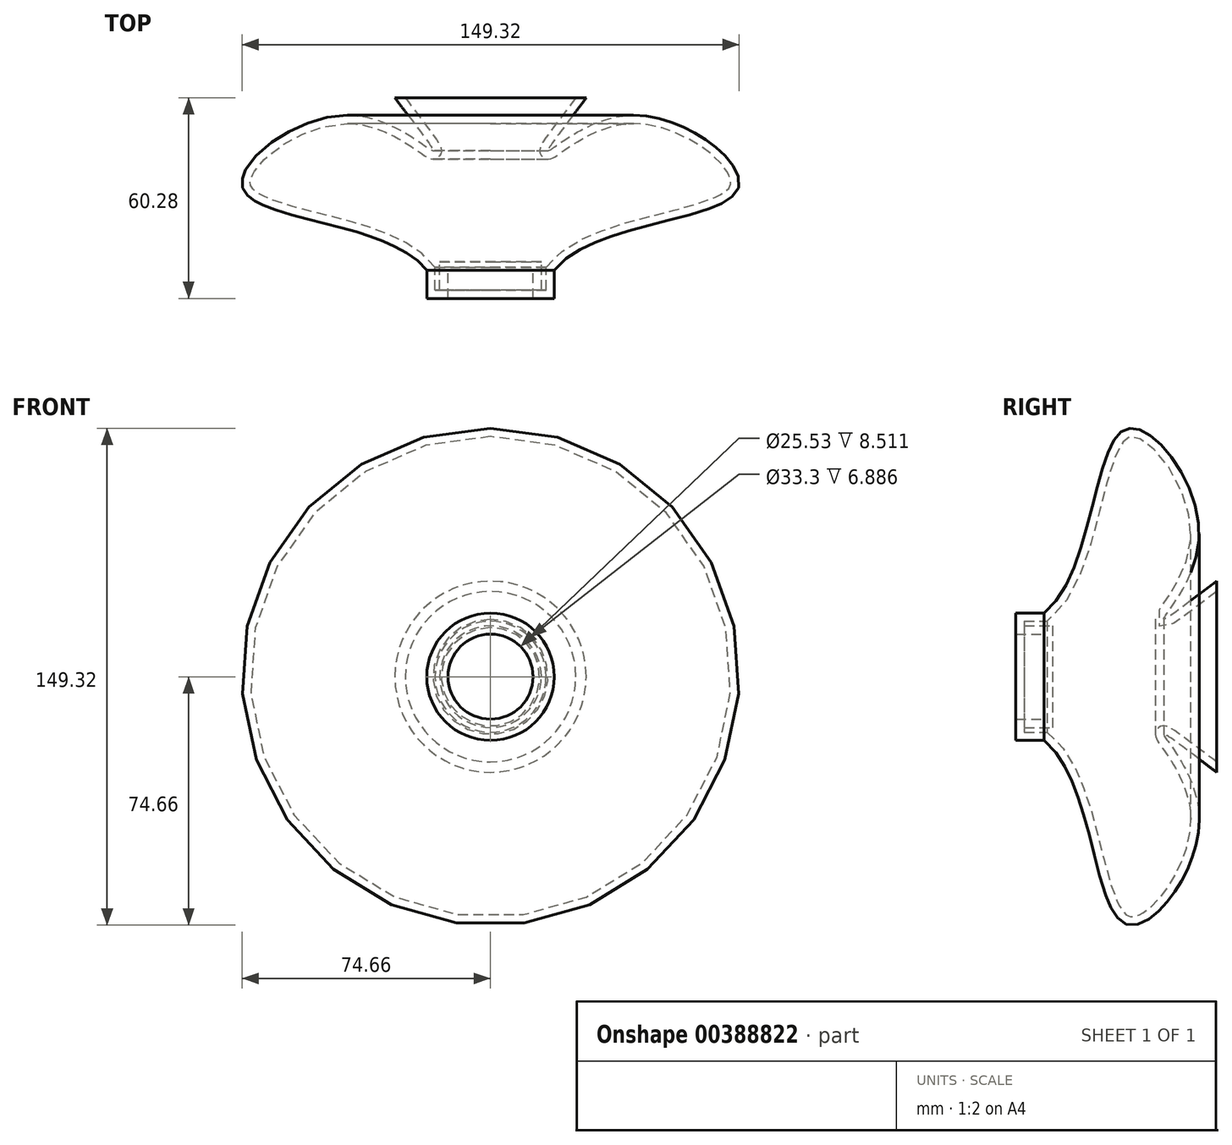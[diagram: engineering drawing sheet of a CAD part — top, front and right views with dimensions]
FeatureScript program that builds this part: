
annotation { "Feature Type Name" : "Feature", "Feature Type Description" : "" }
export const myFeature = defineFeature(function(context is Context, id is Id, definition is map)
    precondition{}
    {
        {
            var Q0;
            Q0=qCreatedBy(makeId("Top.planeOp"),FACE);
            var sketch = newSketch(context, id + "F0", { "sketchPlane" : qUnion([Q0])});
            skLineSegment(sketch, "E0", {"start": v(0, 0) * mm, "end": v(28.72, 0) * mm});
            skLineSegment(sketch, "E1", {"start": v(0, -51.77) * mm, "end": v(12.77, -51.77) * mm});
            skLineSegment(sketch, "E2", {"start": v(12.77, -51.77) * mm, "end": v(12.77, -60.28) * mm});
            skLineSegment(sketch, "E3", {"start": v(12.77, -60.28) * mm, "end": v(19.15, -60.28) * mm});
            skLineSegment(sketch, "E4", {"start": v(19.15, -60.28) * mm, "end": v(19.15, -51.77) * mm});
            skFitSpline(sketch, "E5", {"points": [v(28.72, 0) * mm, v(17.28, -15.9) * mm, v(42.15, -5.26) * mm, v(74.28, -27.44) * mm, v(19.15, -51.77) * mm], "startDerivative": vector(-74.69, -101.23) * mm, "endDerivative": vector(-108.21, -135.6) * mm});
            skLineSegment(sketch, "E6", {"start": v(0, 0) * mm, "end": v(0, -51.77) * mm});
            skSolve(sketch);
        }
        {
            var Q0;
            Q0=makeQuery(id+"F0.imprint","IMPRINT",FACE,{"disambiguationData":[TD([[makeQuery(id+"F0.imprint","IMPRINT",EDGE,{"derivedFrom":sQuery(id+"F0.wireOp",EDGE,"E0")}),-1.0]])]});
            var Q1;
            Q1=sQuery(id+"F0.wireOp",EDGE,"E6");
            revolve(context, id + "F1", {"entities" : qUnion([Q0]), "axis" : qUnion([Q1]), "revolveType" : RevolveType.FULL});
        }
        {
            var Q0;
            Q0=makeQuery(id+"F1.opRevolve","SWEPT_FACE",FACE,{"disambiguationData":[OSD([sQuery(id+"F0.wireOp",EDGE,"E0")])]});
            shell(context, id + "F2", {"entities" : qUnion([Q0]), "thickness" : 2.5 * mm});
        }
    });
